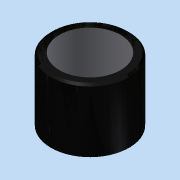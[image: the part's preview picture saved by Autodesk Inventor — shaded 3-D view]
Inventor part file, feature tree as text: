
AUTODESK INVENTOR PART (.ipt)
format: ipt  version: 2015 (Build 190159000, 159)  size: 987,648 bytes
history: native  units: in
note: dims shown in document units (in); Inventor stores cm internally (conversion verified against a paired STEP export)
features: other x6, extrude x2, move_body x2, sketch x2, direct_edit x1, projected_geometry x1
ambient origin geometry x8: Origin, YZ Plane, XZ Plane, XY Plane, X Axis, Y Axis, Z Axis, Center Point
bodies: Solid1 (feature_tree), Solid2 (feature_tree)
feature tree (14):
  other  "Wheel.ipt"
  other  "RingGear.ipt"
  extrude  "Extrusion1"  Depth=0.3937in
  move_body  "Move Body1"
  extrude  "Extrusion2"  TaperAngle=0.0deg  [1 undecoded]
  direct_edit  "Direct Edit1"
  other  "Solid1::Wheel.ipt"
  other  "TaggingFeature1"
  sketch  "Sketch1"  dims[d0=0.3937in]
  other  "Solid1::RingGear.ipt"
  other  "TaggingFeature2"
  sketch  "Sketch2"  dims[d2=0.38in d4=0.44in d6=0.815in d7=0.29in d9=1.025in d10=0.2898in d11=0.36in d13=1.14in d14=0.834in d15=0.0in d17=0.865in d18=0.1in d19=0.296in d20=0.0in d21=0.15in d23=0.0in d24=0.168in d25=0.18in d27=0.05in d28=2.3622in d29=360.0deg d31=0.168in d32=0.18in d34=30.0deg d35=0.09in d36=0.06in d38=0.0in d39=0.05in d40=0.02in d41=2.3622in d42=360.0deg d44=0.08in d47=0.08in d48=0.292in d1=2.5591in d3=0.0in d5=0.0in d8=0.3937in d12=90.0deg d16=0.0in d22=0.0in d26=0.0in d30=0.0in d33=-2.6378in]
  projected_geometry  "Project Cut Edges1"
  move_body  "Move1"
note: 1 required parameter value undecoded (feature->parameter linkage not recoverable at this tier; creation-order binding heuristic only, values carry confidence <= 0.55)
